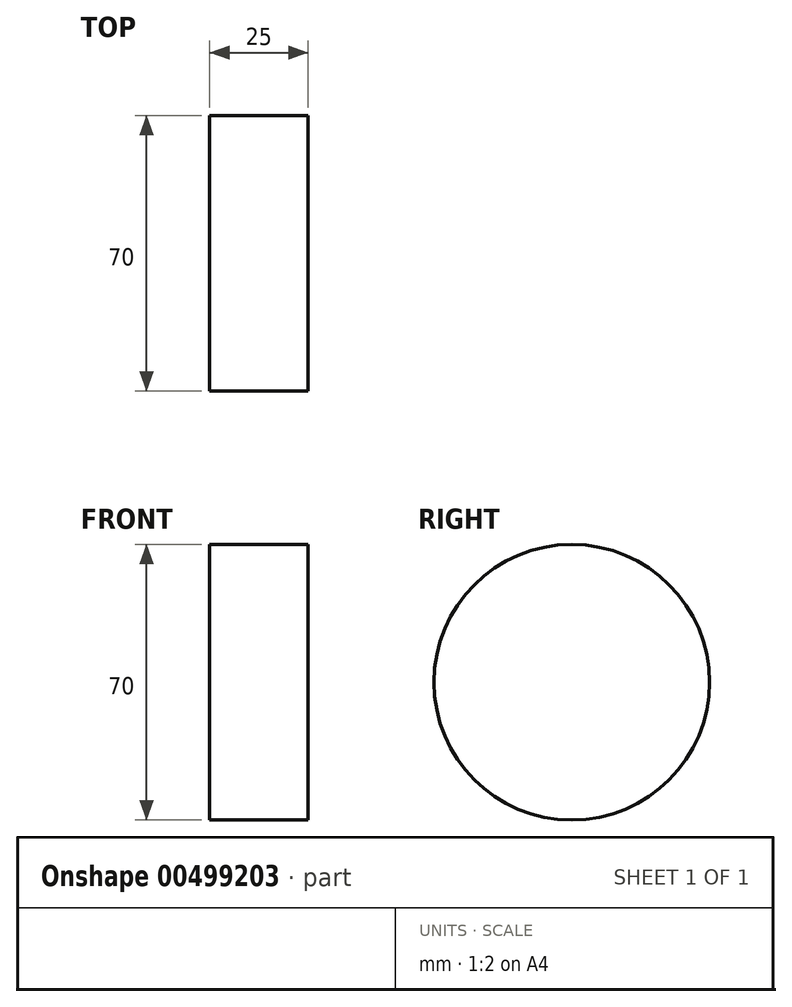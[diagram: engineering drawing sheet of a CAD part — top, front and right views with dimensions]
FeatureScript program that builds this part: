
annotation { "Feature Type Name" : "Feature", "Feature Type Description" : "" }
export const myFeature = defineFeature(function(context is Context, id is Id, definition is map)
    precondition{}
    {
        {
            var Q0;
            Q0=qCreatedBy(makeId("Right.planeOp"),FACE);
            var sketch = newSketch(context, id + "F0", { "sketchPlane" : qUnion([Q0])});
            skCircle(sketch, "E0", {"center": v(0, 0) * mm, "radius": 35 * mm});
            skSolve(sketch);
        }
        {
            var Q0;
            Q0 = qSketchRegion(id + "F0", true);
            extrude(context, id + "F1", {"entities" : qUnion([Q0]), "depth" : 25 * mm});
        }
    });
